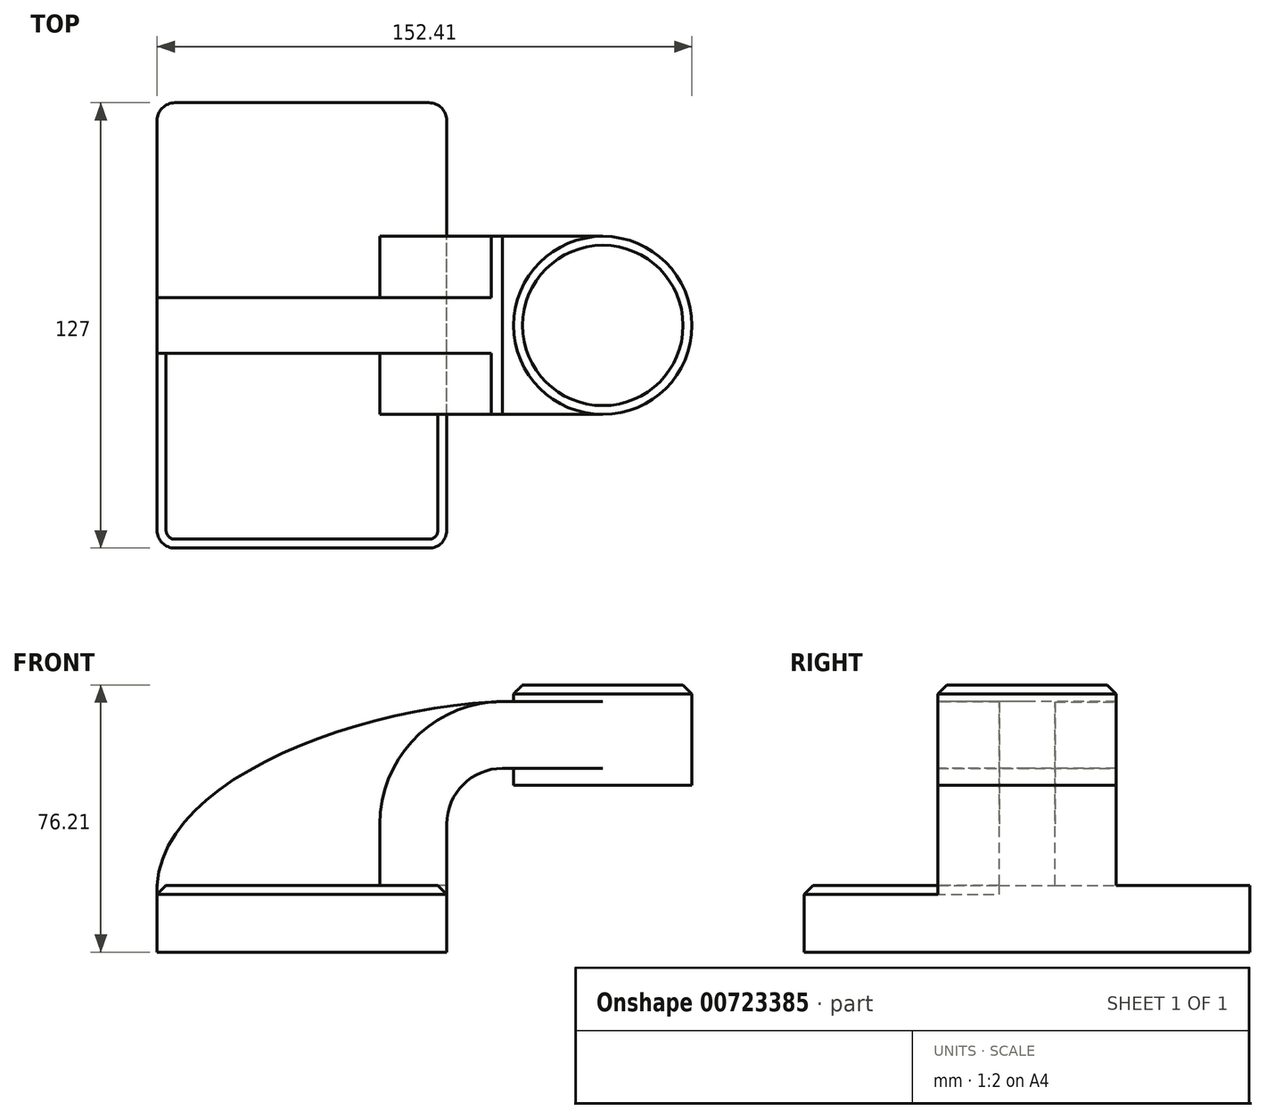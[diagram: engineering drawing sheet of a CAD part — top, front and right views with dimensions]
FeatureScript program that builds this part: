
annotation { "Feature Type Name" : "Feature", "Feature Type Description" : "" }
export const myFeature = defineFeature(function(context is Context, id is Id, definition is map)
    precondition{}
    {
        {
            var Q0;
            Q0=qCreatedBy(makeId("Front.planeOp"),FACE);
            var sketch = newSketch(context, id + "F0", { "sketchPlane" : qUnion([Q0])});
            skLineSegment(sketch, "E0.rect.bottom", {"start": v(-41.28, 9.52) * mm, "end": v(41.28, 9.52) * mm});
            skLineSegment(sketch, "E0.rect.top", {"start": v(-41.28, -9.52) * mm, "end": v(41.28, -9.52) * mm});
            skLineSegment(sketch, "E0.rect.left", {"start": v(-41.28, 9.52) * mm, "end": v(-41.28, -9.52) * mm});
            skLineSegment(sketch, "E0.rect.right", {"start": v(41.28, 9.52) * mm, "end": v(41.28, -9.52) * mm});
            skPoint(sketch, "E0.rect.middle", {"position": v(0, 0) * mm});
            skLineSegment(sketch, "E1", {"start": v(41.28, 9.52) * mm, "end": v(41.28, 27) * mm});
            skArc(sketch, "E2", {"start": v(41.28, 27) * mm, "mid": v(45.92, 38.23) * mm, "end": v(57.15, 42.88) * mm});
            skLineSegment(sketch, "E3", {"start": v(57.15, 42.88) * mm, "end": v(85.72, 42.88) * mm});
            skLineSegment(sketch, "E4.rect.bottom", {"start": v(60.32, 38.1) * mm, "end": v(111.12, 38.1) * mm});
            skLineSegment(sketch, "E4.rect.top", {"start": v(60.32, 66.68) * mm, "end": v(111.12, 66.68) * mm});
            skLineSegment(sketch, "E4.rect.left", {"start": v(60.32, 38.1) * mm, "end": v(60.32, 66.68) * mm});
            skLineSegment(sketch, "E4.rect.right", {"start": v(111.13, 38.1) * mm, "end": v(111.12, 66.68) * mm});
            skPoint(sketch, "E4.rect.middle", {"position": v(85.72, 52.39) * mm});
            skLineSegment(sketch, "E5.0", {"start": v(57.15, 61.93) * mm, "end": v(85.72, 61.93) * mm});
            skArc(sketch, "E5.1", {"start": v(22.23, 27) * mm, "mid": v(32.45, 51.7) * mm, "end": v(57.15, 61.93) * mm});
            skLineSegment(sketch, "E5.2", {"start": v(22.23, 9.52) * mm, "end": v(22.23, 27) * mm});
            skLineSegment(sketch, "E6", {"start": v(85.72, 38.1) * mm, "end": v(85.72, 66.68) * mm});
            skFitSpline(sketch, "E7", {"points": [v(-41.28, 9.53) * mm, v(57.15, 61.93) * mm], "startDerivative": vector(5.2, 92.34) * mm, "endDerivative": vector(120.92, 4.22) * mm});
            skSolve(sketch);
        }
        {
            var Q0;
            Q0=makeQuery(id+"F0.imprint","IMPRINT",FACE,{"disambiguationData":[TD([[makeQuery(id+"F0.imprint","IMPRINT",EDGE,{"derivedFrom":sQuery(id+"F0.wireOp",EDGE,"E0.rect.top")}),1.0]])]});
            extrude(context, id + "F1", {"entities" : qUnion([Q0]), "endBound" : BoundingType.SYMMETRIC, "depth" : 127 * mm});
        }
        {
            var Q0;
            {var subQ9=sQuery(id+"F0.wireOp",EDGE,"E1");Q0=makeQuery(id+"F0.imprint","IMPRINT",FACE,{"disambiguationData":[TD([[makeQuery(id+"F0.imprint","IMPRINT",EDGE,{"derivedFrom":subQ9}),1.0]])]});}
            var Q1;
            {var subQ0=sQuery(id+"F0.wireOp",EDGE,"E6");var subQ1=sQuery(id+"F0.wireOp",EDGE,"E3");var subQ2=makeQuery(id+"F0.imprint","INTERSECT",VERTEX,{"derivedFrom":[subQ1,subQ0]});Q1=makeQuery(id+"F0.imprint","IMPRINT",FACE,{"disambiguationData":[TD([[makeQuery(id+"F0.imprint","IMPRINT",EDGE,{"disambiguationData":[TD([[subQ2,1.0]])],"derivedFrom":subQ1}),1.0]])]});}
            extrude(context, id + "F2", {"entities" : qUnion([Q0, Q1]), "operationType" : NewBodyOperationType.ADD, "endBound" : BoundingType.SYMMETRIC, "depth" : 50.8 * mm});
        }
        {
            var Q0;
            {var subQ3=sQuery(id+"F0.wireOp",EDGE,"E5.2");Q0=makeQuery(id+"F0.imprint","IMPRINT",FACE,{"disambiguationData":[TD([[makeQuery(id+"F0.imprint","IMPRINT",EDGE,{"derivedFrom":subQ3}),1.0]])]});}
            extrude(context, id + "F3", {"entities" : qUnion([Q0]), "operationType" : NewBodyOperationType.ADD, "endBound" : BoundingType.SYMMETRIC, "depth" : 15.88 * mm});
        }
        {
            var Q0;
            {var subQ5=sQuery(id+"F0.wireOp",EDGE,"E4.rect.right");Q0=makeQuery(id+"F0.imprint","IMPRINT",FACE,{"disambiguationData":[TD([[makeQuery(id+"F0.imprint","IMPRINT",EDGE,{"derivedFrom":subQ5}),1.0]])]});}
            var Q1;
            Q1=sQuery(id+"F0.wireOp",EDGE,"E6");
            revolve(context, id + "F4", {"operationType" : NewBodyOperationType.ADD, "entities" : qUnion([Q0]), "axis" : qUnion([Q1]), "revolveType" : RevolveType.FULL});
        }
        {
            var Q0;
            Q0=makeQuery(id+"F1.opExtrude","CAP_EDGE",EDGE,{"disambiguationData":[OSD([sQuery(id+"F0.wireOp",EDGE,"E0.rect.right")])],"isStart":false});
            var Q1;
            Q1=makeQuery(id+"F1.opExtrude","CAP_EDGE",EDGE,{"disambiguationData":[OSD([sQuery(id+"F0.wireOp",EDGE,"E0.rect.left")])],"isStart":false});
            var Q2;
            Q2=makeQuery(id+"F1.opExtrude","CAP_EDGE",EDGE,{"disambiguationData":[OSD([sQuery(id+"F0.wireOp",EDGE,"E0.rect.right")])],"isStart":true});
            var Q3;
            Q3=makeQuery(id+"F1.opExtrude","CAP_EDGE",EDGE,{"disambiguationData":[OSD([sQuery(id+"F0.wireOp",EDGE,"E0.rect.left")])],"isStart":true});
            fillet(context, id + "F5", {"entities" : qUnion([Q0, Q1, Q2, Q3]), "radius" : 5.08 * mm, "tangentPropagation" : true, "allowEdgeOverflow" : false});
        }
        {
            var Q0;
            Q0=makeQuery(id+"F1.opExtrude","CAP_EDGE",EDGE,{"disambiguationData":[OSD([sQuery(id+"F0.wireOp",EDGE,"E0.rect.bottom")])],"isStart":false});
            var Q1;
            Q1=makeQuery(id+"F4.opRevolve","SWEPT_EDGE",EDGE,{"disambiguationData":[OSD([sQuery(id+"F0.wireOp",EDGE,"E4.rect.top"),sQuery(id+"F0.wireOp",EDGE,"E4.rect.right")])]});
            chamfer(context, id + "F6", {"entities" : qUnion([Q0, Q1]), "width" : 2.54 * mm, "tangentPropagation" : true});
        }
    });
